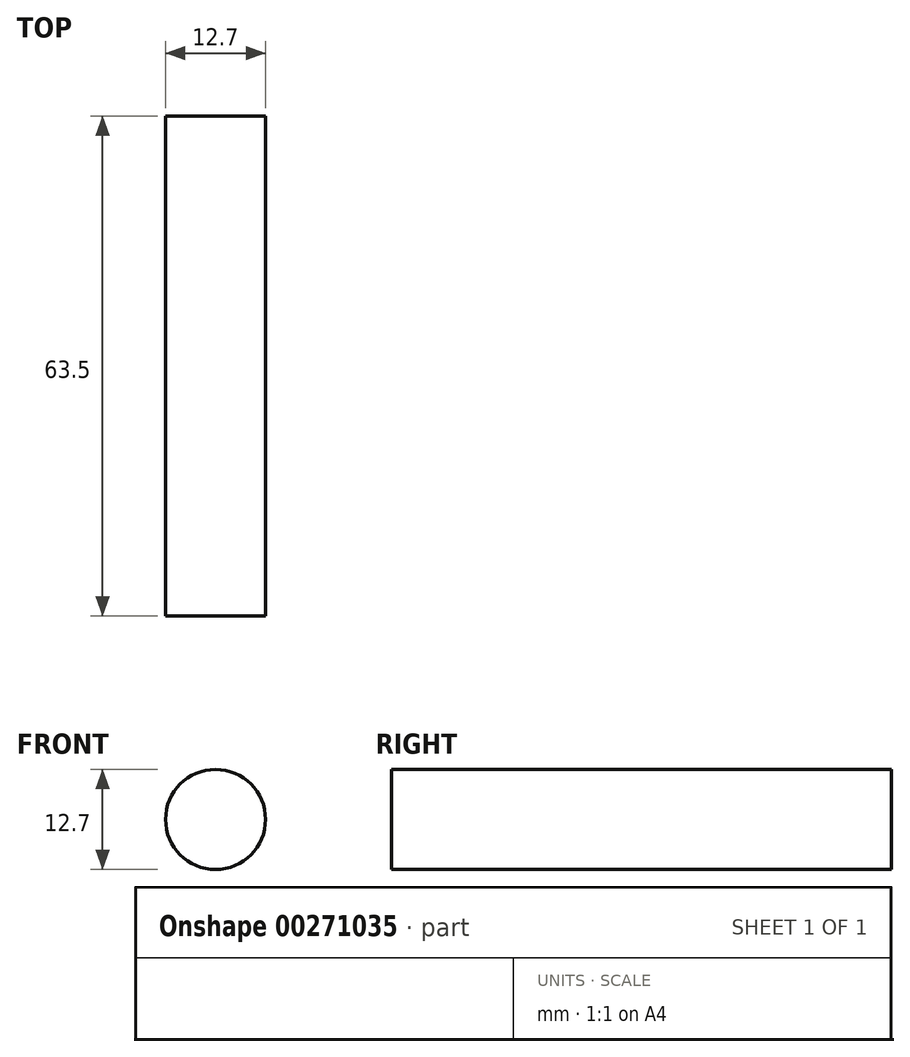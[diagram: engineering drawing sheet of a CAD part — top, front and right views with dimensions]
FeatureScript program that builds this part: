
annotation { "Feature Type Name" : "Feature", "Feature Type Description" : "" }
export const myFeature = defineFeature(function(context is Context, id is Id, definition is map)
    precondition{}
    {
        {
            var Q0;
            Q0=qCreatedBy(makeId("Front.planeOp"),FACE);
            var sketch = newSketch(context, id + "F0", { "sketchPlane" : qUnion([Q0])});
            skCircle(sketch, "E0", {"center": v(0, 0) * mm, "radius": 6.35 * mm});
            skSolve(sketch);
        }
        {
            var Q0;
            Q0 = qSketchRegion(id + "F0", true);
            extrude(context, id + "F1", {"entities" : qUnion([Q0]), "depth" : 63.5 * mm});
        }
    });
